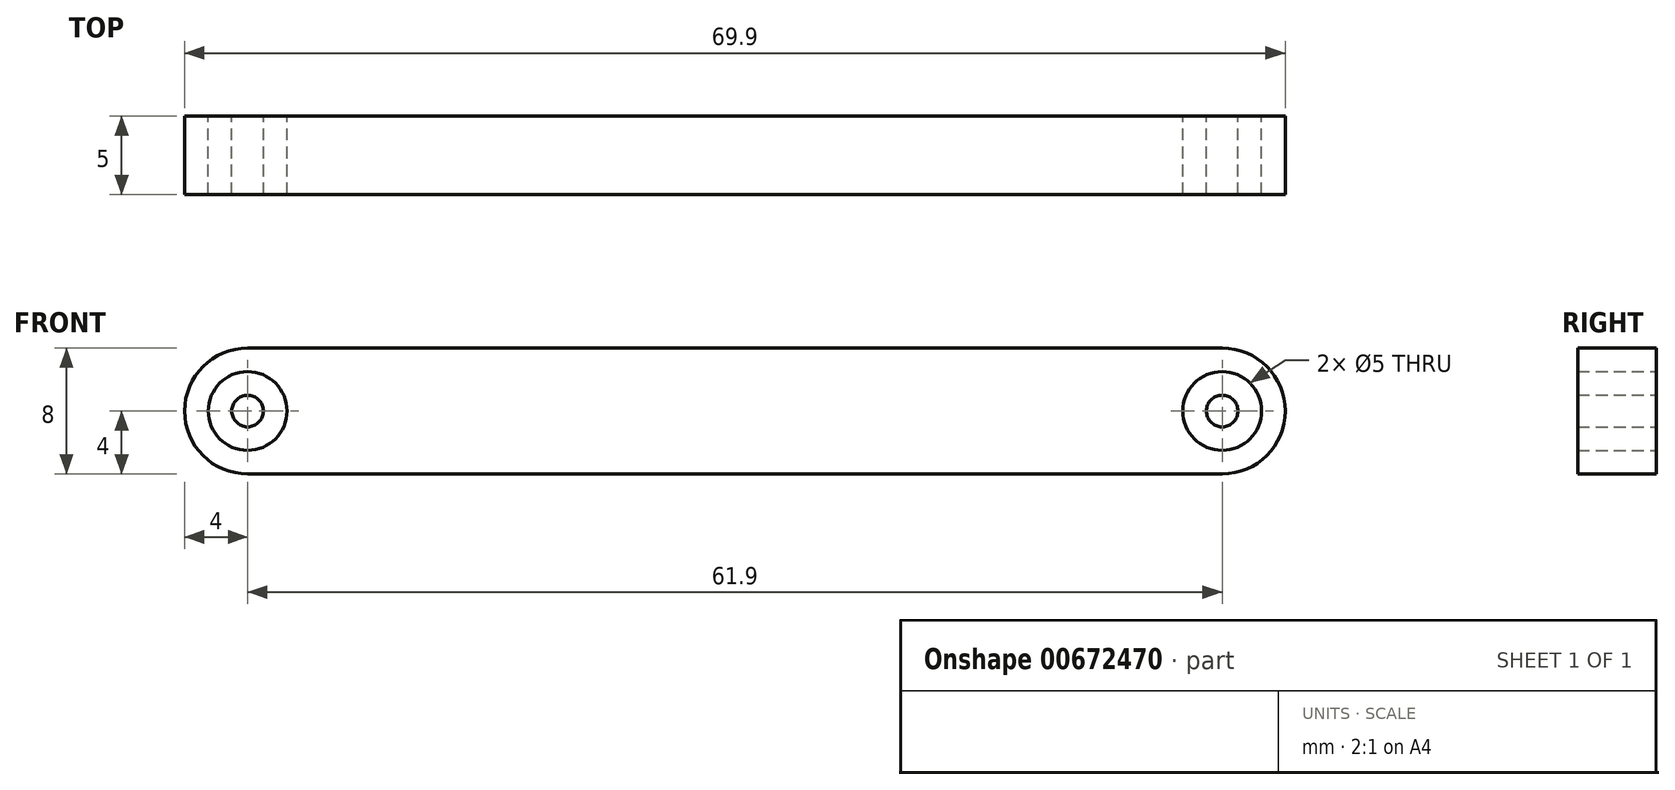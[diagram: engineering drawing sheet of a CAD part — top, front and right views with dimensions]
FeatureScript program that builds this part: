
annotation { "Feature Type Name" : "Feature", "Feature Type Description" : "" }
export const myFeature = defineFeature(function(context is Context, id is Id, definition is map)
    precondition{}
    {
        {
            var Q0;
            Q0=qCreatedBy(makeId("Front.planeOp"),FACE);
            var sketch = newSketch(context, id + "F0", { "sketchPlane" : qUnion([Q0])});
            skArc(sketch, "E0", {"start": v(0, 4) * mm, "mid": v(-4, 0) * mm, "end": v(0, -4) * mm});
            skCircle(sketch, "E1", {"center": v(0, 0) * mm, "radius": 2.5 * mm});
            skArc(sketch, "E2", {"start": v(61.9, -4) * mm, "mid": v(65.9, 0) * mm, "end": v(61.9, 4) * mm});
            skCircle(sketch, "E3", {"center": v(61.9, 0) * mm, "radius": 2.5 * mm});
            skLineSegment(sketch, "E4", {"start": v(0, 4) * mm, "end": v(61.9, 4) * mm});
            skLineSegment(sketch, "E5", {"start": v(0, -4) * mm, "end": v(61.9, -4) * mm});
            skCircle(sketch, "E6", {"center": v(0, 0) * mm, "radius": 1 * mm});
            skCircle(sketch, "E7", {"center": v(61.9, 0) * mm, "radius": 1 * mm});
            skSolve(sketch);
        }
        {
            var Q0;
            Q0=makeQuery(id+"F0.imprint","IMPRINT",FACE,{"disambiguationData":[TD([[makeQuery(id+"F0.imprint","IMPRINT",EDGE,{"derivedFrom":sQuery(id+"F0.wireOp",EDGE,"E0")}),1.0]])]});
            var Q1;
            Q1=makeQuery(id+"F0.imprint","IMPRINT",FACE,{"disambiguationData":[TD([[makeQuery(id+"F0.imprint","IMPRINT",EDGE,{"derivedFrom":sQuery(id+"F0.wireOp",EDGE,"E6")}),1.0]])]});
            var Q2;
            Q2=makeQuery(id+"F0.imprint","IMPRINT",FACE,{"disambiguationData":[TD([[makeQuery(id+"F0.imprint","IMPRINT",EDGE,{"derivedFrom":sQuery(id+"F0.wireOp",EDGE,"E7")}),1.0]])]});
            extrude(context, id + "F1", {"entities" : qUnion([Q0, Q1, Q2]), "endBound" : BoundingType.SYMMETRIC, "depth" : 5 * mm, "offsetDistance" : 25.4 * mm});
        }
    });
